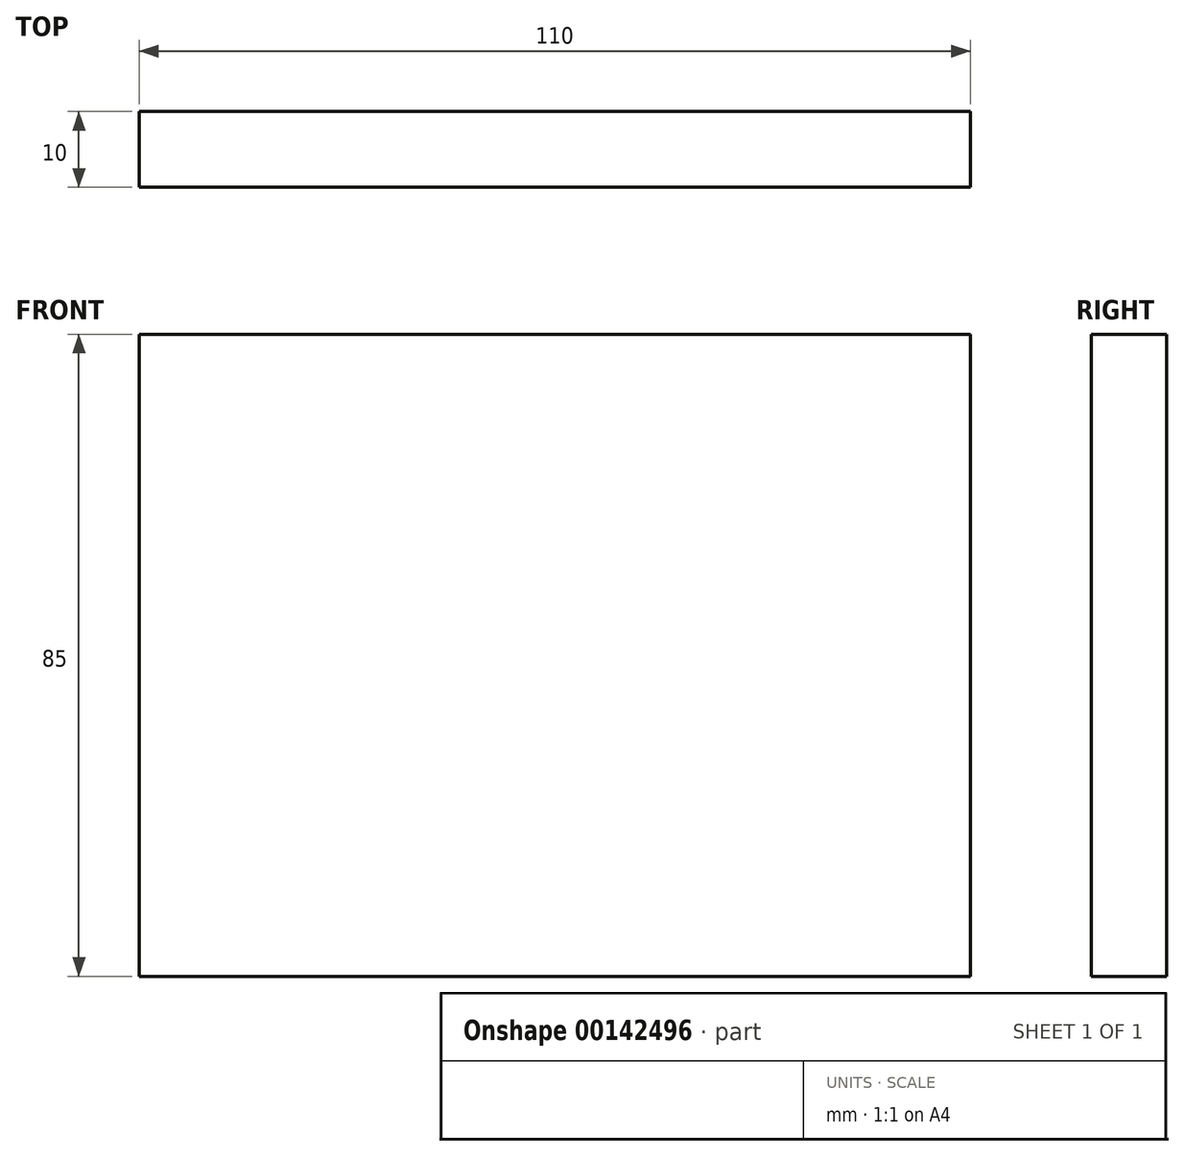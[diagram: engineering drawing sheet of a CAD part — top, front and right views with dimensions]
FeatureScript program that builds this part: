
annotation { "Feature Type Name" : "Feature", "Feature Type Description" : "" }
export const myFeature = defineFeature(function(context is Context, id is Id, definition is map)
    precondition{}
    {
        {
            var Q0;
            Q0=qCreatedBy(makeId("Front.planeOp"),FACE);
            var sketch = newSketch(context, id + "F0", { "sketchPlane" : qUnion([Q0])});
            skLineSegment(sketch, "E0.bottom", {"start": v(-53.69, 85) * mm, "end": v(56.31, 85) * mm});
            skLineSegment(sketch, "E0.top", {"start": v(-53.69, 0) * mm, "end": v(56.31, 0) * mm});
            skLineSegment(sketch, "E0.left", {"start": v(-53.69, 85) * mm, "end": v(-53.69, 0) * mm});
            skLineSegment(sketch, "E0.right", {"start": v(56.31, 85) * mm, "end": v(56.31, 0) * mm});
            skSolve(sketch);
        }
        {
            var Q0;
            Q0 = qSketchRegion(id + "F0", true);
            extrude(context, id + "F1", {"entities" : qUnion([Q0]), "depth" : 10 * mm});
        }
    });
